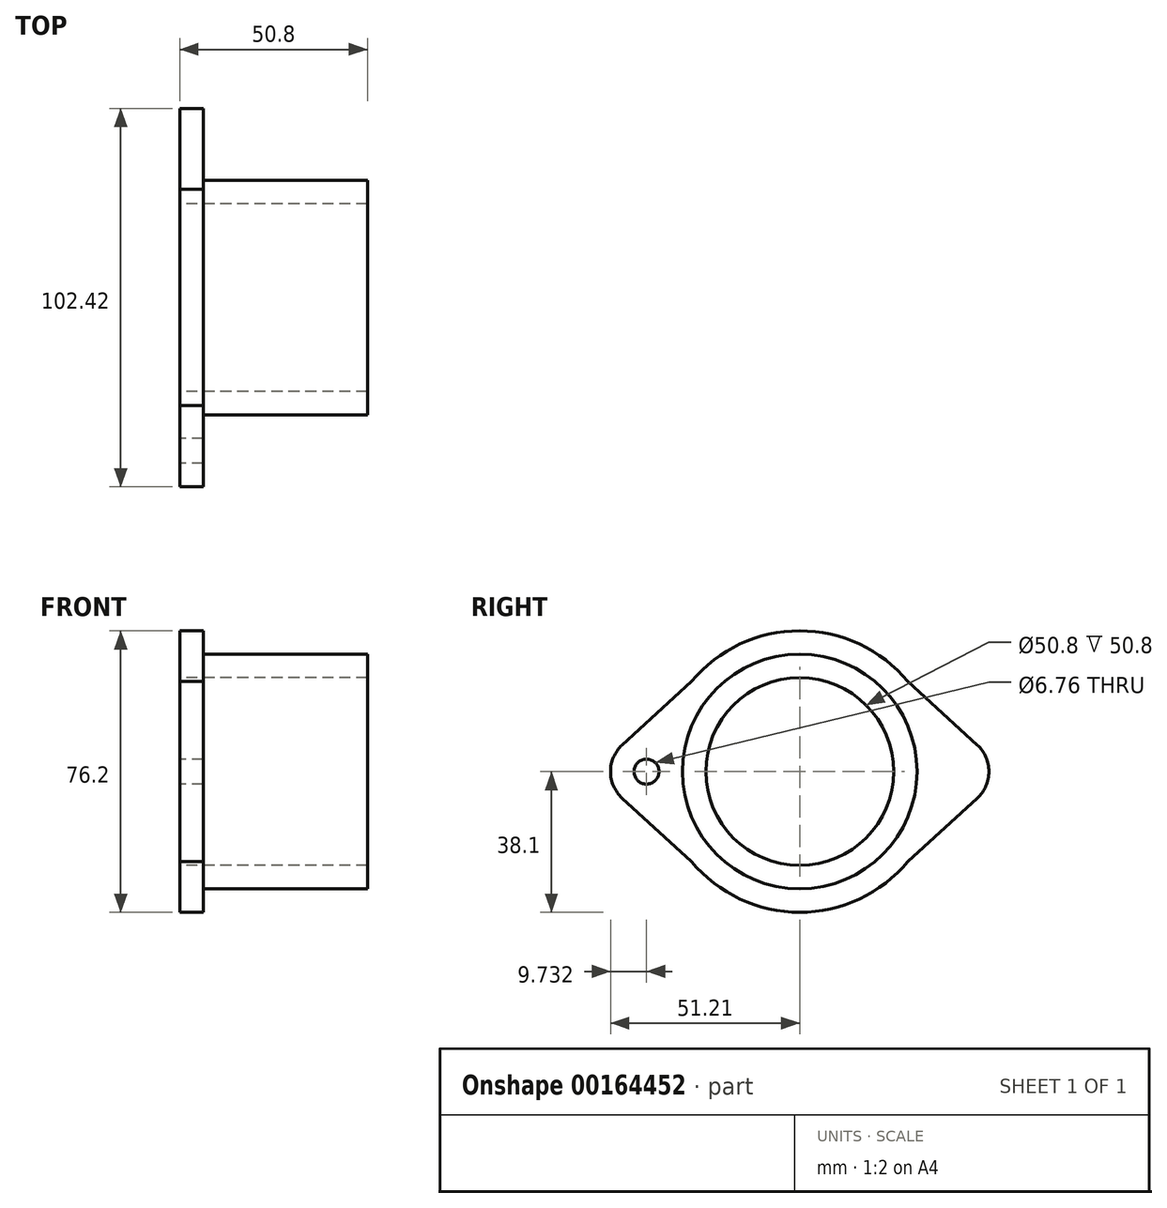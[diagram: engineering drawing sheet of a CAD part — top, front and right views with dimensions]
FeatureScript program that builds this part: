
annotation { "Feature Type Name" : "Feature", "Feature Type Description" : "" }
export const myFeature = defineFeature(function(context is Context, id is Id, definition is map)
    precondition{}
    {
        {
            var Q0;
            Q0=qCreatedBy(makeId("Right.planeOp"),FACE);
            var sketch = newSketch(context, id + "F0", { "sketchPlane" : qUnion([Q0])});
            skCircle(sketch, "E0", {"center": v(0, 0) * mm, "radius": 25.4 * mm});
            skCircle(sketch, "E1", {"center": v(0, 0) * mm, "radius": 31.75 * mm});
            skArc(sketch, "E2", {"start": v(-29.28, -24.38) * mm, "mid": v(0, -38.1) * mm, "end": v(29.28, -24.38) * mm});
            skCircle(sketch, "E3", {"center": v(-41.48, 0) * mm, "radius": 3.38 * mm});
            skArc(sketch, "E4", {"start": v(-48.05, 7.17) * mm, "mid": v(-51.2, 0) * mm, "end": v(-48.05, -7.17) * mm});
            skArc(sketch, "E5.MirrorC", {"start": v(48.05, 7.17) * mm, "mid": v(51.2, 0) * mm, "end": v(48.05, -7.17) * mm});
            skCircle(sketch, "E6.MirrorC", {"center": v(41.48, 0) * mm, "radius": 3.38 * mm});
            skLineSegment(sketch, "E7", {"start": v(-29.28, 24.38) * mm, "end": v(-48.05, 7.17) * mm});
            skLineSegment(sketch, "E8", {"start": v(-29.28, -24.38) * mm, "end": v(-48.05, -7.17) * mm});
            skLineSegment(sketch, "E9.MirrorCS", {"start": v(29.28, 24.38) * mm, "end": v(48.05, 7.17) * mm});
            skLineSegment(sketch, "E10.MirrorCS", {"start": v(29.28, -24.38) * mm, "end": v(48.05, -7.17) * mm});
            skArc(sketch, "E11.trimOffspring", {"start": v(29.28, 24.38) * mm, "mid": v(0, 38.1) * mm, "end": v(-29.28, 24.38) * mm});
            skSolve(sketch);
        }
        {
            var Q0;
            Q0=makeQuery(id+"F0.imprint","IMPRINT",FACE,{"disambiguationData":[TD([[makeQuery(id+"F0.imprint","IMPRINT",EDGE,{"derivedFrom":sQuery(id+"F0.wireOp",EDGE,"E0")}),-1.0]])]});
            extrude(context, id + "F1", {"entities" : qUnion([Q0]), "depth" : 50.8 * mm});
        }
        {
            var Q0;
            {var subQ0=sQuery(id+"F0.wireOp",EDGE,"E7");Q0=makeQuery(id+"F0.imprint","IMPRINT",FACE,{"disambiguationData":[TD([[makeQuery(id+"F0.imprint","IMPRINT",EDGE,{"derivedFrom":subQ0}),1.0]])]});}
            var Q1;
            {var subQ4=sQuery(id+"F0.wireOp",EDGE,"E3");Q1=makeQuery(id+"F0.imprint","IMPRINT",FACE,{"disambiguationData":[TD([[makeQuery(id+"F0.imprint","IMPRINT",EDGE,{"derivedFrom":subQ4}),-1.0]])]});}
            var Q2;
            {var subQ2=sQuery(id+"F0.wireOp",EDGE,"E4");var subQ7=sQuery(id+"F0.wireOp",EDGE,"E1");var subQ8=makeQuery(id+"F0.imprint","INTERSECT",VERTEX,{"derivedFrom":[subQ7,subQ2]});Q2=makeQuery(id+"F0.imprint","IMPRINT",FACE,{"disambiguationData":[TD([[makeQuery(id+"F0.imprint","IMPRINT",EDGE,{"disambiguationData":[TD([[subQ8,1.0]])],"derivedFrom":subQ7}),-1.0]])]});}
            var Q3;
            {var subQ0=sQuery(id+"F0.wireOp",EDGE,"E2");var subQ1=makeQuery(id+"F0.imprint","INTERSECT",VERTEX,{"derivedFrom":[subQ0,sQuery(id+"F0.wireOp",EDGE,"E3")]});Q3=makeQuery(id+"F0.imprint","IMPRINT",FACE,{"disambiguationData":[TD([[makeQuery(id+"F0.imprint","IMPRINT",EDGE,{"disambiguationData":[TD([[subQ1,1.0]])],"derivedFrom":subQ0}),1.0]])]});}
            var Q4;
            {var subQ5=sQuery(id+"F0.wireOp",EDGE,"E4");var subQ7=sQuery(id+"F0.wireOp",EDGE,"E1");var subQ8=makeQuery(id+"F0.imprint","INTERSECT",VERTEX,{"derivedFrom":[subQ7,subQ5]});Q4=makeQuery(id+"F0.imprint","IMPRINT",FACE,{"disambiguationData":[TD([[makeQuery(id+"F0.imprint","IMPRINT",EDGE,{"disambiguationData":[TD([[subQ8,-1.0]])],"derivedFrom":subQ7}),-1.0]])]});}
            var Q5;
            {var subQ0=sQuery(id+"F0.wireOp",EDGE,"E8");Q5=makeQuery(id+"F0.imprint","IMPRINT",FACE,{"disambiguationData":[TD([[makeQuery(id+"F0.imprint","IMPRINT",EDGE,{"derivedFrom":subQ0}),-1.0]])]});}
            var Q6;
            {var subQ0=sQuery(id+"F0.wireOp",EDGE,"E2");var subQ1=makeQuery(id+"F0.imprint","INTERSECT",VERTEX,{"derivedFrom":[subQ0,sQuery(id+"F0.wireOp",EDGE,"E6.MirrorC")]});Q6=makeQuery(id+"F0.imprint","IMPRINT",FACE,{"disambiguationData":[TD([[makeQuery(id+"F0.imprint","IMPRINT",EDGE,{"disambiguationData":[TD([[subQ1,-1.0]])],"derivedFrom":subQ0}),1.0]])]});}
            var Q7;
            {var subQ5=sQuery(id+"F0.wireOp",EDGE,"E6.MirrorC");Q7=makeQuery(id+"F0.imprint","IMPRINT",FACE,{"disambiguationData":[TD([[makeQuery(id+"F0.imprint","IMPRINT",EDGE,{"derivedFrom":subQ5}),1.0]])]});}
            var Q8;
            {var subQ0=sQuery(id+"F0.wireOp",EDGE,"E9.MirrorCS");Q8=makeQuery(id+"F0.imprint","IMPRINT",FACE,{"disambiguationData":[TD([[makeQuery(id+"F0.imprint","IMPRINT",EDGE,{"derivedFrom":subQ0}),-1.0]])]});}
            var Q9;
            {var subQ0=sQuery(id+"F0.wireOp",EDGE,"E10.MirrorCS");Q9=makeQuery(id+"F0.imprint","IMPRINT",FACE,{"disambiguationData":[TD([[makeQuery(id+"F0.imprint","IMPRINT",EDGE,{"derivedFrom":subQ0}),1.0]])]});}
            extrude(context, id + "F2", {"entities" : qUnion([Q0, Q1, Q2, Q3, Q4, Q5, Q6, Q7, Q8, Q9]), "operationType" : NewBodyOperationType.ADD, "depth" : 6.35 * mm});
        }
    });
